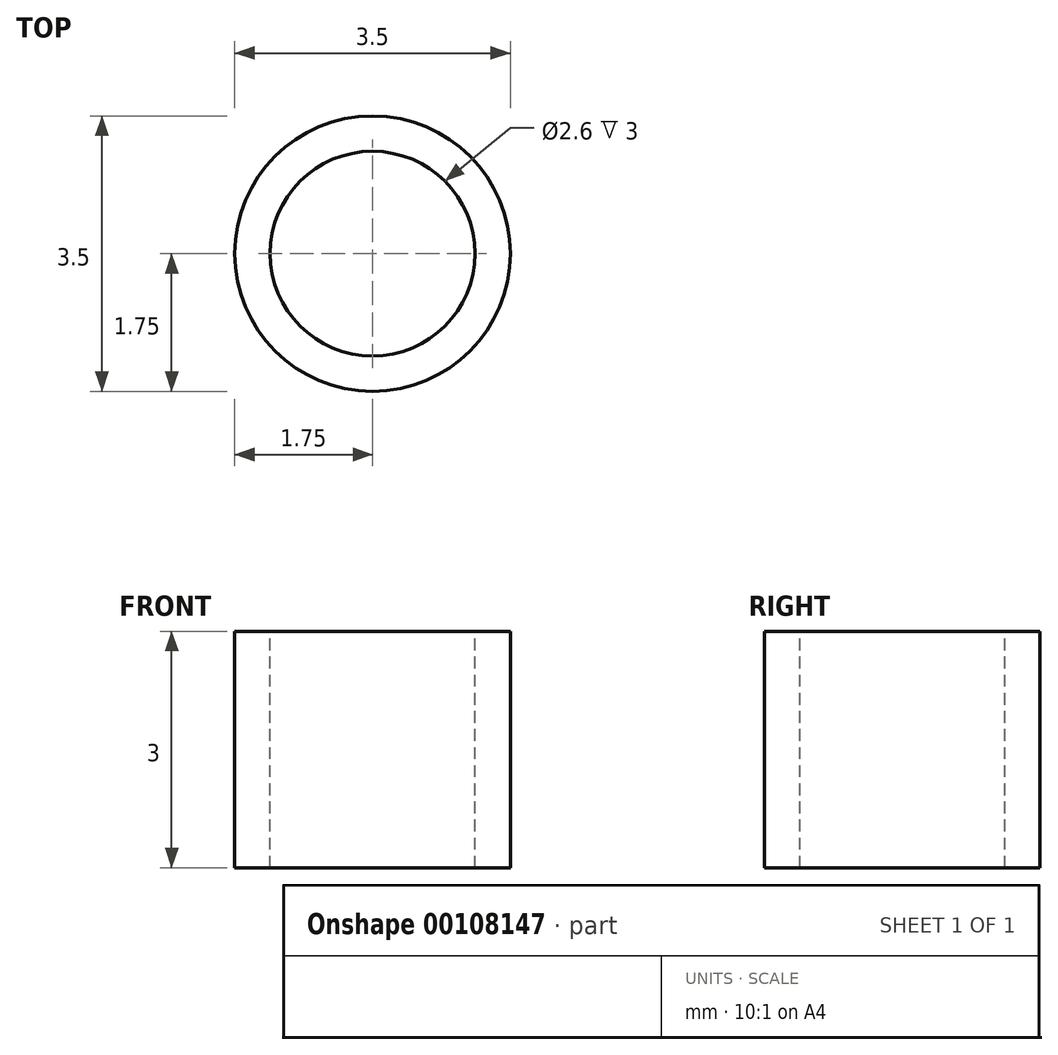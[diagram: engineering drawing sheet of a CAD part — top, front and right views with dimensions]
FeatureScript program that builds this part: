
annotation { "Feature Type Name" : "Feature", "Feature Type Description" : "" }
export const myFeature = defineFeature(function(context is Context, id is Id, definition is map)
    precondition{}
    {
        {
            var Q0;
            Q0=qCreatedBy(makeId("Top.planeOp"),FACE);
            var sketch = newSketch(context, id + "F0", { "sketchPlane" : qUnion([Q0])});
            skCircle(sketch, "E0", {"center": v(0, 0) * mm, "radius": 1.75 * mm});
            skSolve(sketch);
        }
        {
            var Q0;
            Q0=qSketchRegion(id+"F0",true);
            extrude(context, id + "F1", {"entities" : qUnion([Q0]), "depth" : 3 * mm});
        }
        {
            var Q0;
            Q0=makeQuery(id+"F1.opExtrude","CAP_FACE",FACE,{"disambiguationData":[OSD([sQuery(id+"F0.wireOp",EDGE,"E0")])],"isStart":false});
            var sketch = newSketch(context, id + "F2", { "sketchPlane" : qUnion([Q0])});
            skCircle(sketch, "E1", {"center": v(0, 0) * mm, "radius": 1.3 * mm});
            skSolve(sketch);
        }
        {
            var Q0;
            Q0=qSketchRegion(id+"F2",true);
            extrude(context, id + "F3", {"entities" : qUnion([Q0]), "operationType" : NewBodyOperationType.REMOVE, "oppositeDirection" : true, "depth" : 25 * mm});
        }
    });
